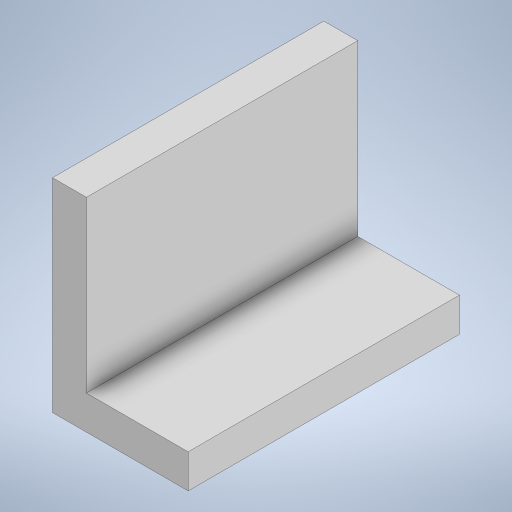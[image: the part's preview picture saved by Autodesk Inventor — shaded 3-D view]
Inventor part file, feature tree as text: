
AUTODESK INVENTOR PART (.ipt)
format: ipt  version: 2023 (Build 270158000, 158)  size: 208,896 bytes
history: native  units: in
note: dims shown in document units (in); Inventor stores cm internally (conversion verified against a paired STEP export)
features: extrude x1, sketch x1
ambient origin geometry x8: Origin, YZ Plane, XZ Plane, XY Plane, X Axis, Y Axis, Z Axis, Center Point
bodies: Solid1 (feature_tree)
feature tree (2):
  extrude  "Extrusion1"  Depth=100.0in
  sketch  "Sketch1"  dims[d3=150.0in d4=100.0in d5=25.0in d6=75.0in d7=200.0in d8=0.0in]
